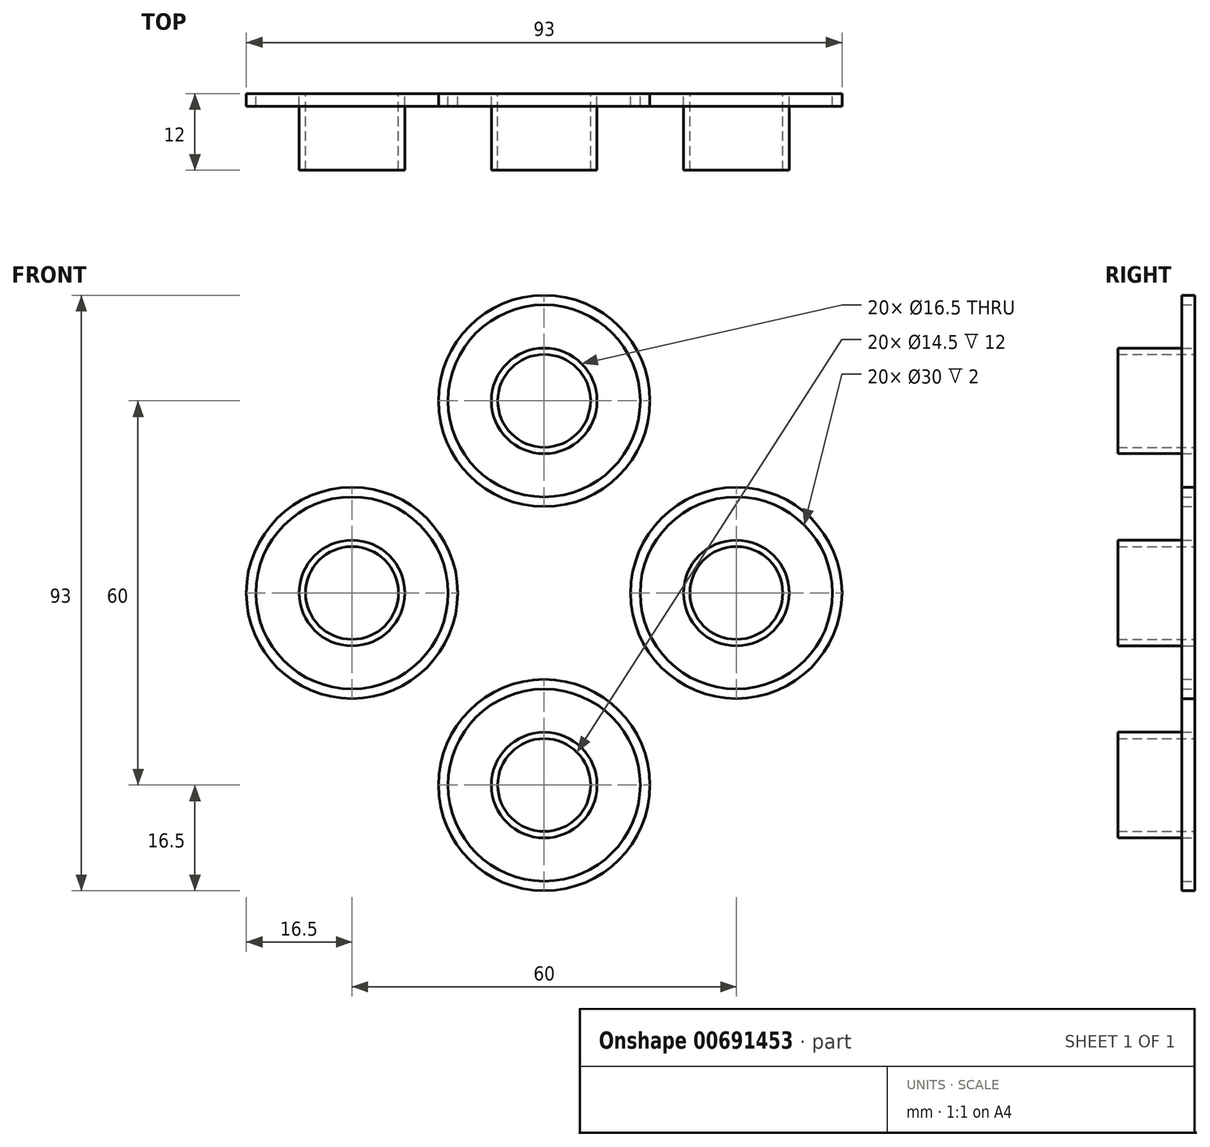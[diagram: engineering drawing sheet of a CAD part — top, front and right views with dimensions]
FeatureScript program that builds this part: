
annotation { "Feature Type Name" : "Feature", "Feature Type Description" : "" }
export const myFeature = defineFeature(function(context is Context, id is Id, definition is map)
    precondition{}
    {
        {
            var Q0;
            Q0=qCreatedBy(makeId("Front.planeOp"),FACE);
            var sketch = newSketch(context, id + "F0", { "sketchPlane" : qUnion([Q0])});
            skCircle(sketch, "E0", {"center": v(0, 0) * mm, "radius": 50 * mm});
            skCircle(sketch, "E1", {"center": v(0, 30) * mm, "radius": 16.5 * mm});
            skCircle(sketch, "E2", {"center": v(0, -30) * mm, "radius": 16.5 * mm});
            skCircle(sketch, "E3", {"center": v(-30, 0) * mm, "radius": 16.5 * mm});
            skCircle(sketch, "E4", {"center": v(30, 0) * mm, "radius": 16.5 * mm});
            skCircle(sketch, "E5", {"center": v(-30, 0) * mm, "radius": 15 * mm});
            skCircle(sketch, "E6", {"center": v(0, -30) * mm, "radius": 15 * mm});
            skCircle(sketch, "E7", {"center": v(30, 0) * mm, "radius": 15 * mm});
            skCircle(sketch, "E8", {"center": v(0, 30) * mm, "radius": 15 * mm});
            skCircle(sketch, "E9", {"center": v(-30, 0) * mm, "radius": 8.25 * mm});
            skCircle(sketch, "E10", {"center": v(0, 30) * mm, "radius": 8.25 * mm});
            skCircle(sketch, "E11", {"center": v(30, 0) * mm, "radius": 8.25 * mm});
            skCircle(sketch, "E12", {"center": v(0, -30) * mm, "radius": 8.25 * mm});
            skCircle(sketch, "E13", {"center": v(0, 30) * mm, "radius": 7.25 * mm});
            skCircle(sketch, "E14", {"center": v(-30, 0) * mm, "radius": 7.25 * mm});
            skCircle(sketch, "E15", {"center": v(0, -30) * mm, "radius": 7.25 * mm});
            skCircle(sketch, "E16", {"center": v(30, 0) * mm, "radius": 0.5 * mm});
            skCircle(sketch, "E17", {"center": v(30, 0) * mm, "radius": 7.25 * mm});
            skSolve(sketch);
        }
        {
            var Q0;
            Q0=makeQuery(id+"F0.imprint","IMPRINT",FACE,{"disambiguationData":[TD([[makeQuery(id+"F0.imprint","IMPRINT",EDGE,{"derivedFrom":sQuery(id+"F0.wireOp",EDGE,"E9")}),1.0]])]});
            var Q1;
            Q1=makeQuery(id+"F0.imprint","IMPRINT",FACE,{"disambiguationData":[TD([[makeQuery(id+"F0.imprint","IMPRINT",EDGE,{"derivedFrom":sQuery(id+"F0.wireOp",EDGE,"E12")}),1.0]])]});
            var Q2;
            Q2=makeQuery(id+"F0.imprint","IMPRINT",FACE,{"disambiguationData":[TD([[makeQuery(id+"F0.imprint","IMPRINT",EDGE,{"derivedFrom":sQuery(id+"F0.wireOp",EDGE,"E11")}),1.0]])]});
            var Q3;
            Q3=makeQuery(id+"F0.imprint","IMPRINT",FACE,{"disambiguationData":[TD([[makeQuery(id+"F0.imprint","IMPRINT",EDGE,{"derivedFrom":sQuery(id+"F0.wireOp",EDGE,"E10")}),1.0]])]});
            extrude(context, id + "F1", {"entities" : qUnion([Q0, Q1, Q2, Q3]), "depth" : 12 * mm, "offsetDistance" : 25 * mm});
        }
        {
            var Q0;
            Q0=makeQuery(id+"F0.imprint","IMPRINT",FACE,{"disambiguationData":[TD([[makeQuery(id+"F0.imprint","IMPRINT",EDGE,{"derivedFrom":sQuery(id+"F0.wireOp",EDGE,"E5")}),1.0]])]});
            var Q1;
            Q1=makeQuery(id+"F0.imprint","IMPRINT",FACE,{"disambiguationData":[TD([[makeQuery(id+"F0.imprint","IMPRINT",EDGE,{"derivedFrom":sQuery(id+"F0.wireOp",EDGE,"E6")}),1.0]])]});
            var Q2;
            Q2=makeQuery(id+"F0.imprint","IMPRINT",FACE,{"disambiguationData":[TD([[makeQuery(id+"F0.imprint","IMPRINT",EDGE,{"derivedFrom":sQuery(id+"F0.wireOp",EDGE,"E7")}),1.0]])]});
            var Q3;
            Q3=makeQuery(id+"F0.imprint","IMPRINT",FACE,{"disambiguationData":[TD([[makeQuery(id+"F0.imprint","IMPRINT",EDGE,{"derivedFrom":sQuery(id+"F0.wireOp",EDGE,"E8")}),1.0]])]});
            extrude(context, id + "F2", {"entities" : qUnion([Q0, Q1, Q2, Q3]), "depth" : 2 * mm, "offsetDistance" : 25 * mm});
        }
        {
            var Q0;
            Q0=makeQuery(id+"F0.imprint","IMPRINT",FACE,{"disambiguationData":[TD([[makeQuery(id+"F0.imprint","IMPRINT",EDGE,{"derivedFrom":sQuery(id+"F0.wireOp",EDGE,"E4")}),1.0]])]});
            var Q1;
            Q1=makeQuery(id+"F0.imprint","IMPRINT",FACE,{"disambiguationData":[TD([[makeQuery(id+"F0.imprint","IMPRINT",EDGE,{"derivedFrom":sQuery(id+"F0.wireOp",EDGE,"E2")}),1.0]])]});
            var Q2;
            Q2=makeQuery(id+"F0.imprint","IMPRINT",FACE,{"disambiguationData":[TD([[makeQuery(id+"F0.imprint","IMPRINT",EDGE,{"derivedFrom":sQuery(id+"F0.wireOp",EDGE,"E3")}),1.0]])]});
            var Q3;
            Q3=makeQuery(id+"F0.imprint","IMPRINT",FACE,{"disambiguationData":[TD([[makeQuery(id+"F0.imprint","IMPRINT",EDGE,{"derivedFrom":sQuery(id+"F0.wireOp",EDGE,"E1")}),1.0]])]});
            extrude(context, id + "F3", {"entities" : qUnion([Q0, Q1, Q2, Q3]), "depth" : 2 * mm, "offsetDistance" : 25 * mm});
        }
    });
